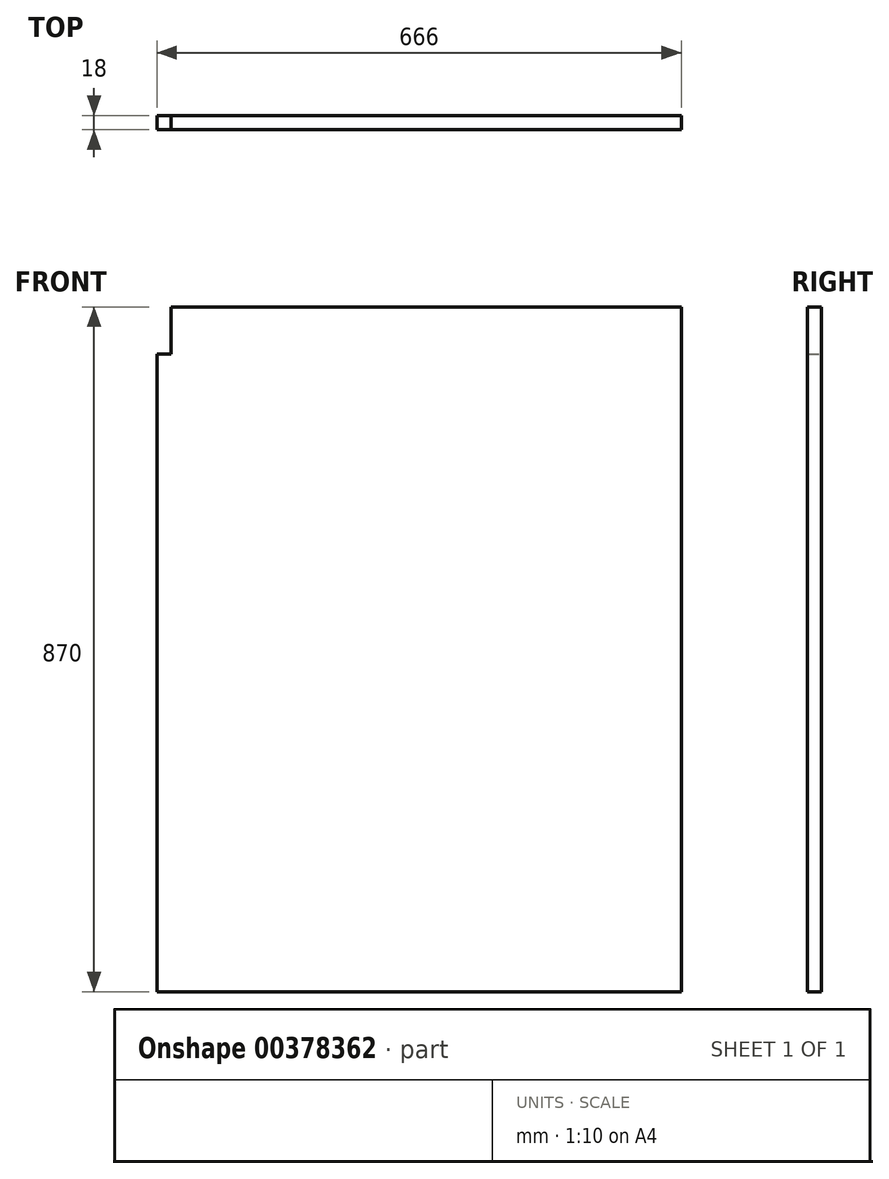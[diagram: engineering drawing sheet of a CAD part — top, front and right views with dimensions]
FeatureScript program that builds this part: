
annotation { "Feature Type Name" : "Feature", "Feature Type Description" : "" }
export const myFeature = defineFeature(function(context is Context, id is Id, definition is map)
    precondition{}
    {
        {
            var Q0;
            Q0=qCreatedBy(makeId("Front.planeOp"),FACE);
            var sketch = newSketch(context, id + "F0", { "sketchPlane" : qUnion([Q0])});
            skLineSegment(sketch, "E0.bottom", {"start": v(333, 435) * mm, "end": v(-315, 435) * mm});
            skLineSegment(sketch, "E0.top", {"start": v(333, -435) * mm, "end": v(-333, -435) * mm});
            skLineSegment(sketch, "E0.left", {"start": v(333, 435) * mm, "end": v(333, -435) * mm});
            skLineSegment(sketch, "E0.right", {"start": v(-333, 375) * mm, "end": v(-333, -435) * mm});
            skPoint(sketch, "E0.middle", {"position": v(0, 0) * mm});
            skLineSegment(sketch, "E1", {"start": v(-315, 435) * mm, "end": v(-315, 375) * mm});
            skLineSegment(sketch, "E2", {"start": v(-315, 375) * mm, "end": v(-333, 375) * mm});
            skSolve(sketch);
        }
        {
            var Q0;
            Q0=makeQuery(id+"F0.imprint","IMPRINT",FACE,{"disambiguationData":[TD([[makeQuery(id+"F0.imprint","IMPRINT",EDGE,{"derivedFrom":sQuery(id+"F0.wireOp",EDGE,"E0.bottom")}),1.0]])]});
            extrude(context, id + "F1", {"entities" : qUnion([Q0]), "depth" : 18 * mm});
        }
    });
